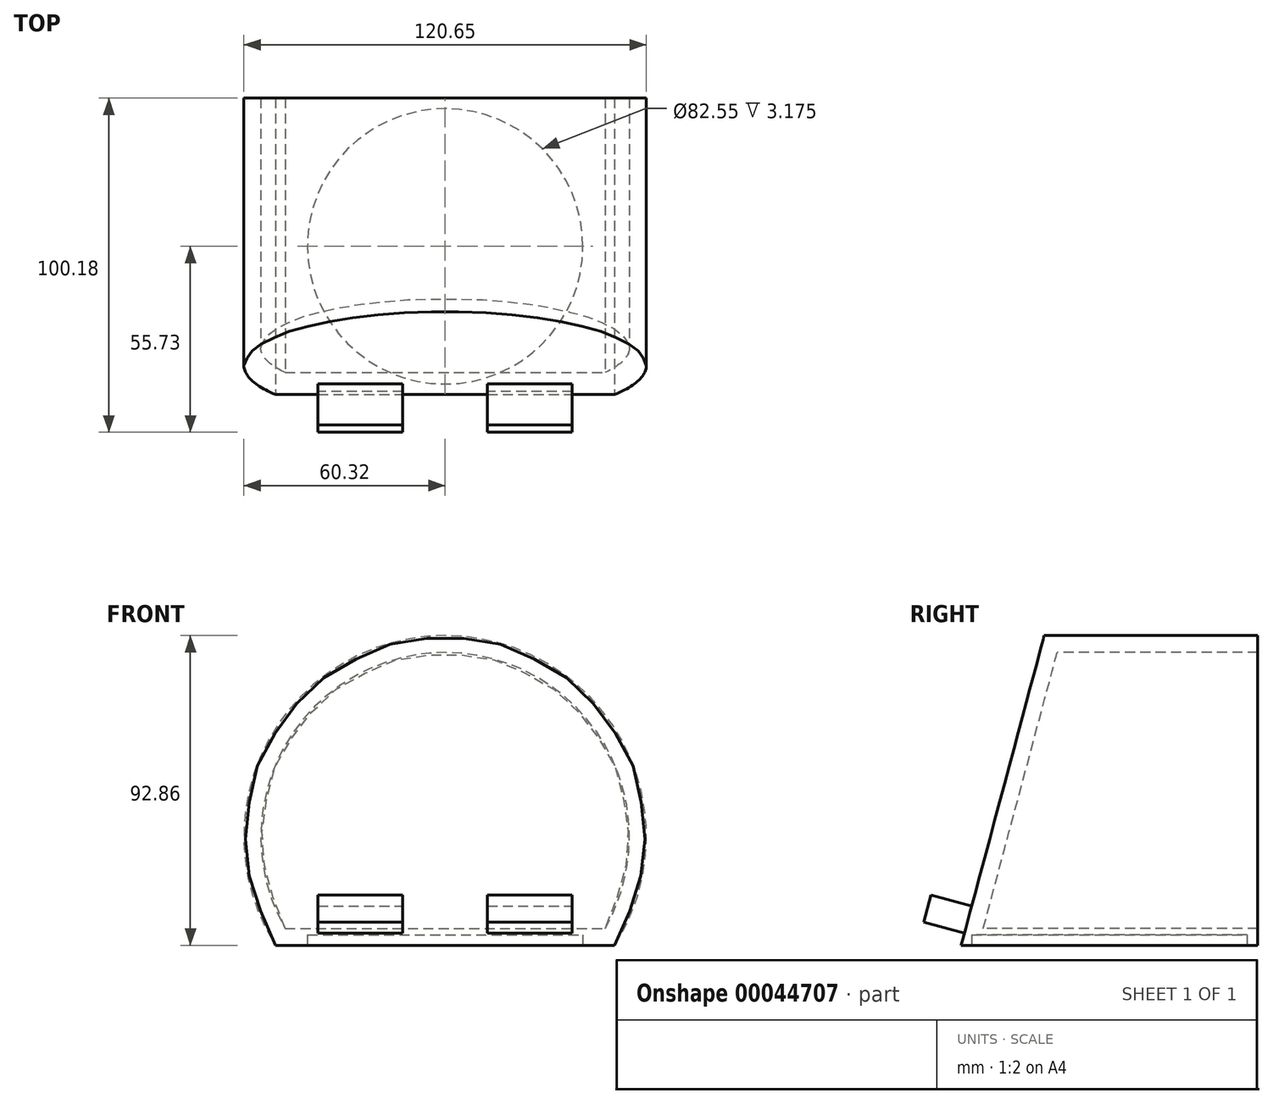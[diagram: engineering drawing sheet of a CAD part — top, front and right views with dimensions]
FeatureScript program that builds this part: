
annotation { "Feature Type Name" : "Feature", "Feature Type Description" : "" }
export const myFeature = defineFeature(function(context is Context, id is Id, definition is map)
    precondition{}
    {
        {
            var Q0;
            Q0=qCreatedBy(makeId("Front.planeOp"),FACE);
            var sketch = newSketch(context, id + "F0", { "sketchPlane" : qUnion([Q0])});
            skArc(sketch, "E0", {"start": v(50.8, -32.53) * mm, "mid": v(0, 60.33) * mm, "end": v(-50.8, -32.53) * mm});
            skLineSegment(sketch, "E1", {"start": v(-50.8, -32.53) * mm, "end": v(50.8, -32.53) * mm});
            skPoint(sketch, "E2", {"position": v(0, 60.33) * mm});
            skSolve(sketch);
        }
        {
            var Q0;
            Q0=makeQuery(id+"F0.imprint","IMPRINT",FACE,{"disambiguationData":[TD([[makeQuery(id+"F0.imprint","IMPRINT",EDGE,{"derivedFrom":sQuery(id+"F0.wireOp",EDGE,"E0")}),1.0]])]});
            extrude(context, id + "F1", {"entities" : qUnion([Q0]), "oppositeDirection" : true, "depth" : 88.9 * mm});
        }
        {
            var Q0;
            Q0=qCreatedBy(makeId("Right.planeOp"),FACE);
            cPlane(context, id + "F2", {"entities" : qUnion([Q0]), "cplaneType" : CPlaneType.OFFSET, "offset" : 152.4 * mm, "width" : 152.4 * mm, "height" : 152.4 * mm});
        }
        {
            var Q0;
            Q0=qCreatedBy(id+"F2.planeOp",FACE);
            var sketch = newSketch(context, id + "F3", { "sketchPlane" : qUnion([Q0])});
            skLineSegment(sketch, "E3", {"start": v(0, 60.33) * mm, "end": v(0, -32.53) * mm});
            skLineSegment(sketch, "E4", {"start": v(0, -32.53) * mm, "end": v(24.88, 60.33) * mm});
            skLineSegment(sketch, "E5", {"start": v(0, 60.32) * mm, "end": v(24.88, 60.33) * mm});
            skSolve(sketch);
        }
        {
            var Q0;
            Q0 = qSketchRegion(id + "F3", true);
            extrude(context, id + "F4", {"entities" : qUnion([Q0]), "operationType" : NewBodyOperationType.REMOVE, "endBound" : BoundingType.THROUGH_ALL, "oppositeDirection" : true, "depth" : 25.4 * mm});
        }
        {
            var Q0;
            Q0=makeQuery(id+"F1.opExtrude","CAP_FACE",FACE,{"disambiguationData":[OSD([sQuery(id+"F0.wireOp",EDGE,"E0"),sQuery(id+"F0.wireOp",EDGE,"64e2c584-68c5-4fe9-a456-2bde2caee502"),sQuery(id+"F0.wireOp",EDGE,"314fc7e3-a9c9-4159-8d63-4ef420e372bf"),sQuery(id+"F0.wireOp",EDGE,"659888e8-aab7-4405-bd76-f06789a58717"),sQuery(id+"F0.wireOp",EDGE,"411348ec-b6aa-4610-a185-24452d4e7edd"),sQuery(id+"F0.wireOp",EDGE,"07d1d67d-fa07-45b8-97cb-13fbaf7f95fb"),sQuery(id+"F0.wireOp",EDGE,"a6fc16c2-20e9-41ec-8969-a2a8412490ed"),sQuery(id+"F0.wireOp",EDGE,"539a6e51-4a87-4d87-912b-7e798f45d0ce"),sQuery(id+"F0.wireOp",EDGE,"2f298690-df94-4da9-89d6-d1c171136101.sketch_text.stroke-41"),sQuery(id+"F0.wireOp",EDGE,"E1")])],"isStart":false});
            shell(context, id + "F5", {"entities" : qUnion([Q0]), "thickness" : 5.08 * mm});
        }
        {
            var Q0;
            Q0=makeQuery(id+"F4.boolean.opBoolean","COPY",FACE,{"derivedFrom":makeQuery(id+"F4.opExtrude","SWEPT_FACE",FACE,{"disambiguationData":[OSD([sQuery(id+"F3.wireOp",EDGE,"E4")])]})});
            var sketch = newSketch(context, id + "F6", { "sketchPlane" : qUnion([Q0])});
            skLineSegment(sketch, "E6", {"start": v(-12.7, -27.62) * mm, "end": v(-38.1, -27.62) * mm});
            skLineSegment(sketch, "E7", {"start": v(38.1, -27.62) * mm, "end": v(12.7, -27.62) * mm});
            skLineSegment(sketch, "E8", {"start": v(-38.1, -27.62) * mm, "end": v(-38.1, -19.23) * mm});
            skLineSegment(sketch, "E9", {"start": v(-38.1, -19.23) * mm, "end": v(-12.7, -19.23) * mm});
            skLineSegment(sketch, "E10", {"start": v(-12.7, -19.23) * mm, "end": v(-12.7, -27.62) * mm});
            skLineSegment(sketch, "E11", {"start": v(12.7, -27.62) * mm, "end": v(12.7, -19.23) * mm});
            skLineSegment(sketch, "E12", {"start": v(12.7, -19.23) * mm, "end": v(38.1, -19.23) * mm});
            skLineSegment(sketch, "E13", {"start": v(38.1, -19.23) * mm, "end": v(38.1, -27.62) * mm});
            skSolve(sketch);
        }
        {
            var Q0;
            Q0=makeQuery(id+"F6.imprint","IMPRINT",FACE,{"disambiguationData":[TD([[makeQuery(id+"F6.imprint","IMPRINT",EDGE,{"derivedFrom":sQuery(id+"F6.wireOp",EDGE,"E6")}),-1.0]])]});
            var Q1;
            Q1=makeQuery(id+"F6.imprint","IMPRINT",FACE,{"disambiguationData":[TD([[makeQuery(id+"F6.imprint","IMPRINT",EDGE,{"derivedFrom":sQuery(id+"F6.wireOp",EDGE,"E7")}),-1.0]])]});
            extrude(context, id + "F7", {"entities" : qUnion([Q0, Q1]), "operationType" : NewBodyOperationType.ADD, "depth" : 12.7 * mm});
        }
        {
            var Q0;
            Q0=makeQuery(id+"F1.opExtrude","SWEPT_FACE",FACE,{"disambiguationData":[OSD([sQuery(id+"F0.wireOp",EDGE,"E1")])]});
            var sketch = newSketch(context, id + "F8", { "sketchPlane" : qUnion([Q0])});
            skLineSegment(sketch, "E14", {"start": v(-50.8, -44.45) * mm, "end": v(50.8, -44.45) * mm});
            skPoint(sketch, "E15", {"position": v(0, -44.45) * mm});
            skCircle(sketch, "E16", {"center": v(0, -44.45) * mm, "radius": 41.28 * mm});
            skSolve(sketch);
        }
        {
            var Q0;
            Q0 = qSketchRegion(id + "F8", true);
            extrude(context, id + "F9", {"entities" : qUnion([Q0]), "operationType" : NewBodyOperationType.REMOVE, "oppositeDirection" : true, "depth" : 3.17 * mm});
        }
    });
